# Revit family: Hose_Box-With_Door-Dual_Check-Acorn-816X_Series
name_source: partatom
category: Plumbing Fixtures
units: mm (PartAtom-declared; Revit-internal decimal feet)

## family parameters
Cut with Voids When Loaded = Yes
Host = Face
OmniClass Number = 23.65.55.14
OmniClass Title = Valves for Liquid Services
Part Type = Normal
Room Calculation Point = No
Round Connector Dimension = Use Diameter
Shared = Yes

## types (8) — shared parameters
Assembly Code = D2010800
CW Connection = No
Default Elevation = 0"
Description = Dual Check Non-Freeze Hose Box with Door
Finish = Stainless Steel-Acorn-Polished Satin
HW Connection = No
IAPMO Compliance = Meets ASSE standards 1052, 1053 and 1019-B
Installation Instruction Link = https://www.acorneng.com
Installation Type = Wall Mounted
Manufacturer = Acorn
Material = Stainless Steel-Acorn-Polished Satin
Model = 8160
NPT Connection Diameter = 3/4"
Product Documentation Link = https://www.acorneng.com
Product Page URL = https://www.acorneng.com
Tempered Water Connection = Yes
URL = https://www.acorneng.com
Vent Connection = No
Waste Connection = No
Waste Connection Diameter = 3/4"
Waste Fitting Material = Cast Bronze-Acorn-Stainless Steel
Width = 10 1/2"
cUPC Compliant = Yes
zero-valued in all types: CWFU, HWFU, WFU

## per-type parameters (varying)
| type | 8160- Dual Check Hydrant Recessed Hose Box and Door | 8161- Dual Check Hydrant Recessed Hose Box Less Door | Wall Depth |
| 8160 - 4" Wall Thickness | Yes | No | 4" |
| 8160 - 6" Wall Thickness | Yes | No | 6" |
| 8160 - 8" Wall Thickness | Yes | No | 8" |
| 8160 - 12" Wall Thickness | Yes | No | 12" |
| 8161 - 4" Wall Thickness | No | Yes | 4" |
| 8161 - 8" Wall Thickness | No | Yes | 8" |
| 8161 - 6" Wall Thickness | No | Yes | 6" |
| 8161 - 12" Wall Thickness | No | Yes | 12" |

## geometry (parser evidence)
native form markers: Sweep x2
no freeform markers — native parametric forms only
